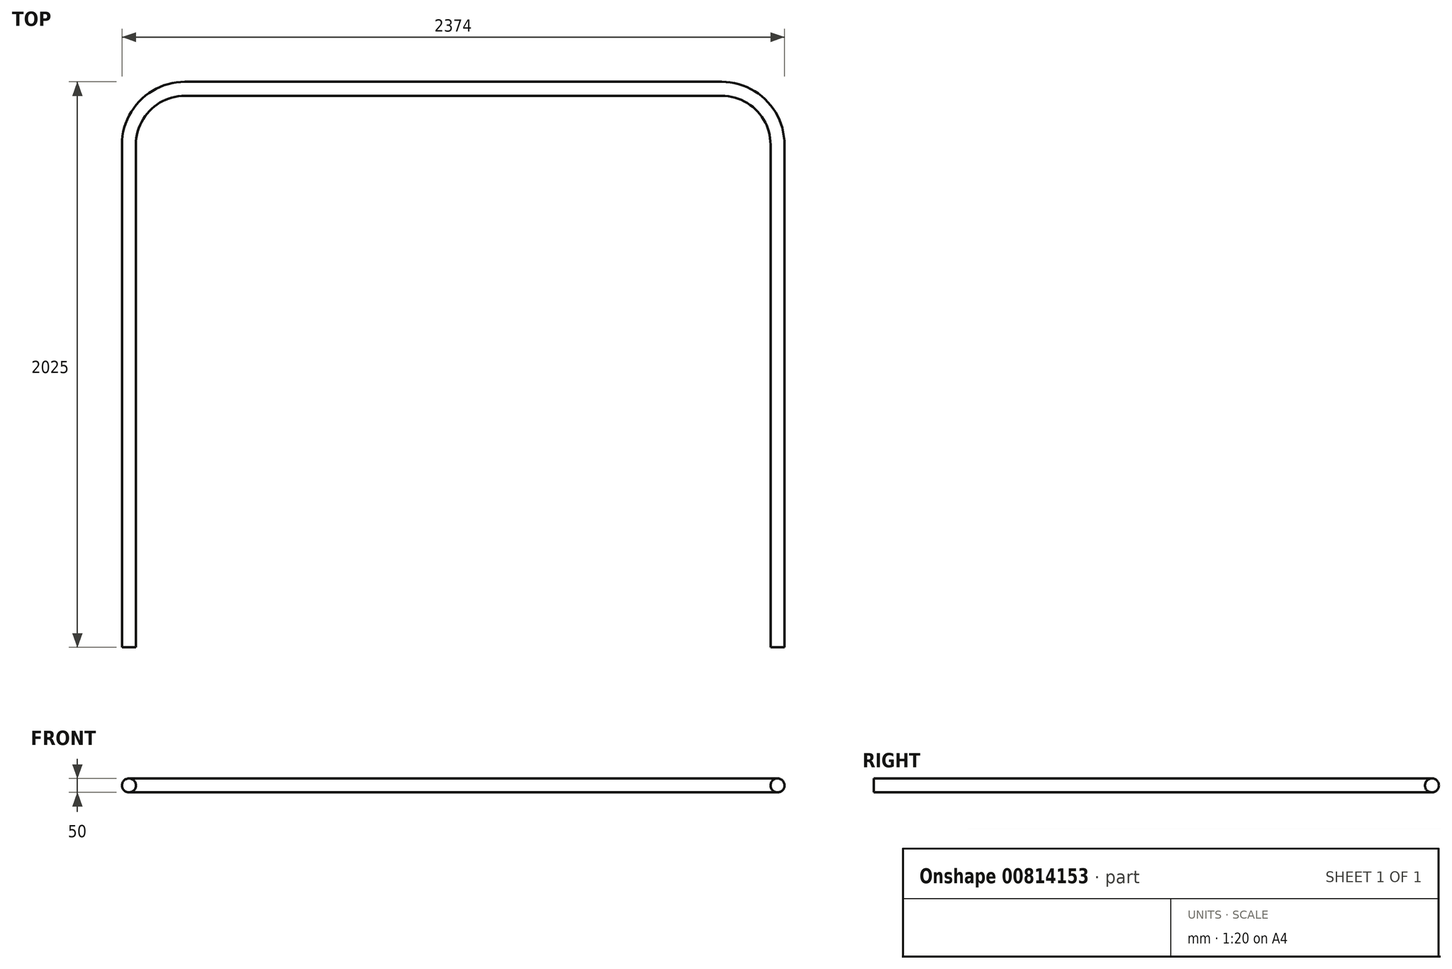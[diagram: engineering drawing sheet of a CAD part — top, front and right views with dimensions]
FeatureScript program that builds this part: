
annotation { "Feature Type Name" : "Feature", "Feature Type Description" : "" }
export const myFeature = defineFeature(function(context is Context, id is Id, definition is map)
    precondition{}
    {
        {
            var Q0;
            Q0=qCreatedBy(makeId("Top.planeOp"),FACE);
            var sketch = newSketch(context, id + "F0", { "sketchPlane" : qUnion([Q0])});
            skLineSegment(sketch, "E0.top", {"start": v(-900, 2000) * mm, "end": v(1024, 2000) * mm});
            skLineSegment(sketch, "E0.left", {"start": v(-1100, 0) * mm, "end": v(-1100, 1800) * mm});
            skLineSegment(sketch, "E0.right", {"start": v(1224, 0) * mm, "end": v(1224, 1800) * mm});
            skPoint(sketch, "E1.visualSharp", {"position": v(-1100, 2000) * mm});
            skArc(sketch, "E1.filletArc", {"start": v(-900, 2000) * mm, "mid": v(-1041.42, 1941.42) * mm, "end": v(-1100, 1800) * mm});
            skPoint(sketch, "E2.visualSharp", {"position": v(1224, 2000) * mm});
            skArc(sketch, "E2.filletArc", {"start": v(1224, 1800) * mm, "mid": v(1165.42, 1941.42) * mm, "end": v(1024, 2000) * mm});
            skSolve(sketch);
        }
        {
            var Q0;
            Q0=qCreatedBy(makeId("Front.planeOp"),FACE);
            var sketch = newSketch(context, id + "F1", { "sketchPlane" : qUnion([Q0])});
            skPoint(sketch, "E3.0", {"position": v(-1100, 0) * mm});
            skCircle(sketch, "E4", {"center": v(-1100, 0) * mm, "radius": 25 * mm});
            skSolve(sketch);
        }
        {
            var Q0;
            Q0=makeQuery(id+"F1.imprint","IMPRINT",FACE,{"disambiguationData":[TD([[makeQuery(id+"F1.imprint","IMPRINT",EDGE,{"derivedFrom":sQuery(id+"F1.wireOp",EDGE,"E4")}),1.0]])]});
            var Q1;
            Q1=sQuery(id+"F0.wireOp",EDGE,"E0.left");
            var Q2;
            Q2=sQuery(id+"F0.wireOp",EDGE,"E1.filletArc");
            var Q3;
            Q3=sQuery(id+"F0.wireOp",EDGE,"E0.top");
            var Q4;
            Q4=sQuery(id+"F0.wireOp",EDGE,"E2.filletArc");
            var Q5;
            Q5=sQuery(id+"F0.wireOp",EDGE,"E0.right");
            sweep(context, id + "F2", {"profiles" : qUnion([Q0]), "path" : qUnion([Q1, Q2, Q3, Q4, Q5])});
        }
    });
